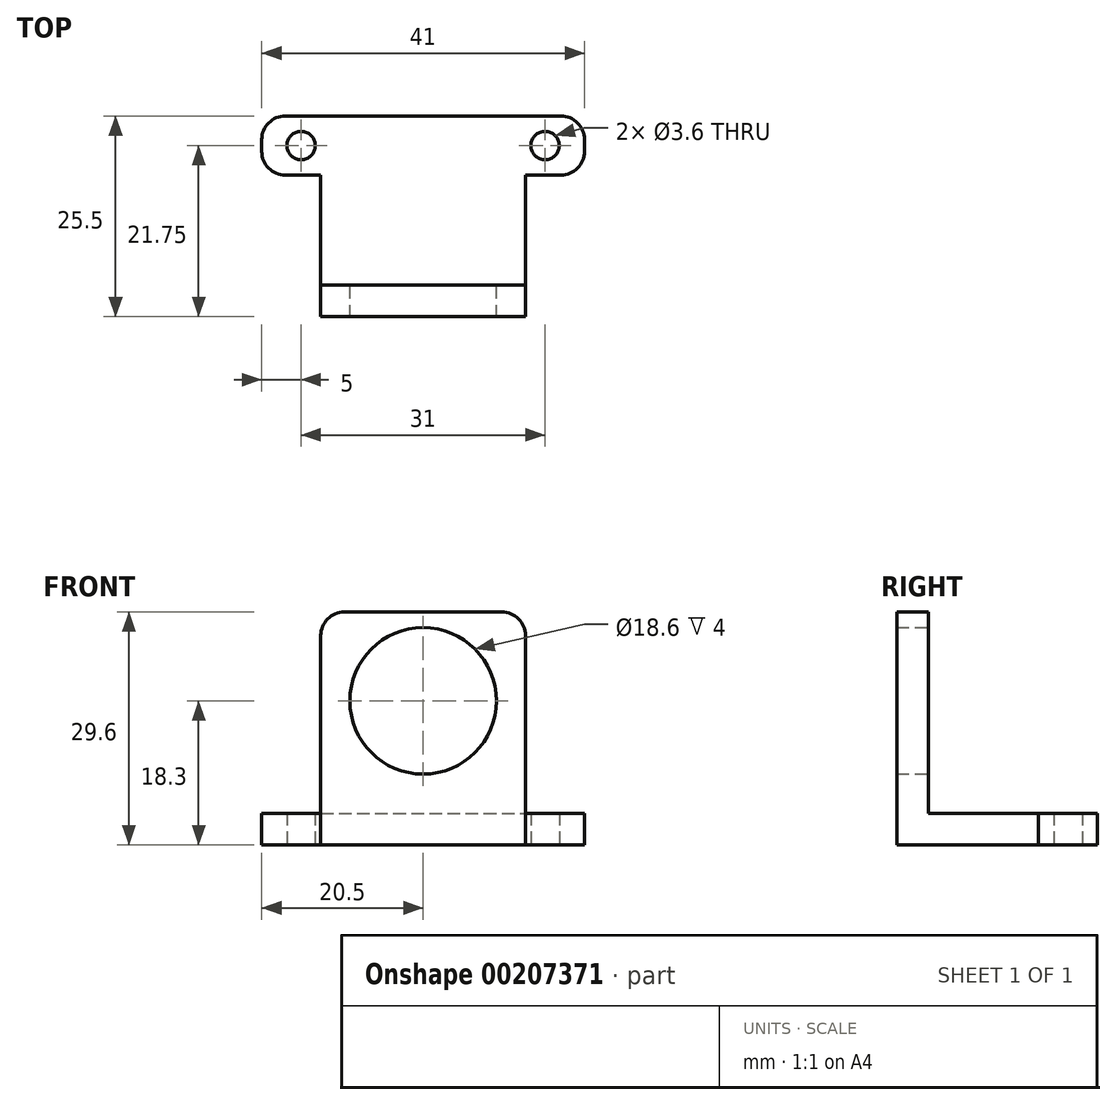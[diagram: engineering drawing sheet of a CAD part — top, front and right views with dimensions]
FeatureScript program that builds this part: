
annotation { "Feature Type Name" : "Feature", "Feature Type Description" : "" }
export const myFeature = defineFeature(function(context is Context, id is Id, definition is map)
    precondition{}
    {
        {
            var Q0;
            Q0=qCreatedBy(makeId("Top.planeOp"),FACE);
            var sketch = newSketch(context, id + "F0", { "sketchPlane" : qUnion([Q0])});
            skLineSegment(sketch, "E0.bottom", {"start": v(-41, 7.5) * mm, "end": v(0, 7.5) * mm});
            skLineSegment(sketch, "E0.top", {"start": v(-41, 0) * mm, "end": v(0, 0) * mm});
            skLineSegment(sketch, "E0.left", {"start": v(-41, 7.5) * mm, "end": v(-41, 0) * mm});
            skLineSegment(sketch, "E0.right", {"start": v(0, 7.5) * mm, "end": v(0, 0) * mm});
            skCircle(sketch, "E1", {"center": v(-36, 3.75) * mm, "radius": 1.8 * mm});
            skPoint(sketch, "E1.centerSnap0", {"position": v(-41, 3.75) * mm});
            skCircle(sketch, "E2", {"center": v(-5, 3.75) * mm, "radius": 1.8 * mm});
            skPoint(sketch, "E2.centerSnap0", {"position": v(0, 3.75) * mm});
            skLineSegment(sketch, "E3", {"start": v(-36, 3.75) * mm, "end": v(-5, 3.75) * mm, "construction": true});
            skPoint(sketch, "E4", {"position": v(-20.5, 7.5) * mm});
            skPoint(sketch, "E5", {"position": v(-20.5, 3.75) * mm});
            skLineSegment(sketch, "E6", {"start": v(-33.5, 0) * mm, "end": v(-33.5, -18) * mm});
            skLineSegment(sketch, "E7", {"start": v(-33.5, -18) * mm, "end": v(-7.5, -18) * mm});
            skLineSegment(sketch, "E8", {"start": v(-7.5, -18) * mm, "end": v(-7.5, 0) * mm});
            skPoint(sketch, "E9", {"position": v(-20.5, -18) * mm});
            skLineSegment(sketch, "E10", {"start": v(-33.5, -14) * mm, "end": v(-7.5, -14) * mm});
            skSolve(sketch);
        }
        {
            var Q0;
            Q0=makeQuery(id+"F0.imprint","IMPRINT",FACE,{"disambiguationData":[TD([[makeQuery(id+"F0.imprint","IMPRINT",EDGE,{"derivedFrom":sQuery(id+"F0.wireOp",EDGE,"E0.bottom")}),-1.0]])]});
            var Q1;
            {var subQ5=sQuery(id+"F0.wireOp",EDGE,"E10");Q1=makeQuery(id+"F0.imprint","IMPRINT",FACE,{"disambiguationData":[TD([[makeQuery(id+"F0.imprint","IMPRINT",EDGE,{"derivedFrom":subQ5}),1.0]])]});}
            extrude(context, id + "F1", {"entities" : qUnion([Q0, Q1]), "depth" : 4 * mm});
        }
        {
            var Q0;
            {var subQ0=sQuery(id+"F0.wireOp",EDGE,"E7");Q0=makeQuery(id+"F0.imprint","IMPRINT",FACE,{"disambiguationData":[TD([[makeQuery(id+"F0.imprint","IMPRINT",EDGE,{"derivedFrom":subQ0}),1.0]])]});}
            extrude(context, id + "F2", {"entities" : qUnion([Q0]), "operationType" : NewBodyOperationType.ADD, "depth" : 29.6 * mm});
        }
        {
            var Q0;
            Q0=makeQuery(id+"F2.opExtrude","SWEPT_FACE",FACE,{"disambiguationData":[OSD([sQuery(id+"F0.wireOp",EDGE,"E10")])]});
            var sketch = newSketch(context, id + "F3", { "sketchPlane" : qUnion([Q0])});
            skCircle(sketch, "E11", {"center": v(20.5, 18.3) * mm, "radius": 9.3 * mm});
            skSolve(sketch);
        }
        {
            var Q0;
            Q0=makeQuery(id+"F3.imprint","IMPRINT",FACE,{"disambiguationData":[TD([[makeQuery(id+"F3.imprint","IMPRINT",EDGE,{"derivedFrom":sQuery(id+"F3.wireOp",EDGE,"E11")}),1.0]])]});
            extrude(context, id + "F4", {"entities" : qUnion([Q0]), "operationType" : NewBodyOperationType.REMOVE, "endBound" : BoundingType.UP_TO_NEXT, "oppositeDirection" : true, "depth" : 25 * mm});
        }
        {
            var Q0;
            Q0=makeQuery(id+"F1.opExtrude","SWEPT_EDGE",EDGE,{"disambiguationData":[OSD([sQuery(id+"F0.wireOp",EDGE,"E0.top"),sQuery(id+"F0.wireOp",EDGE,"E0.right")])]});
            var Q1;
            Q1=makeQuery(id+"F1.opExtrude","SWEPT_EDGE",EDGE,{"disambiguationData":[OSD([sQuery(id+"F0.wireOp",EDGE,"E0.bottom"),sQuery(id+"F0.wireOp",EDGE,"E0.right")])]});
            var Q2;
            Q2=makeQuery(id+"F1.opExtrude","SWEPT_EDGE",EDGE,{"disambiguationData":[OSD([sQuery(id+"F0.wireOp",EDGE,"E0.top"),sQuery(id+"F0.wireOp",EDGE,"E0.left")])]});
            var Q3;
            Q3=makeQuery(id+"F1.opExtrude","SWEPT_EDGE",EDGE,{"disambiguationData":[OSD([sQuery(id+"F0.wireOp",EDGE,"E0.bottom"),sQuery(id+"F0.wireOp",EDGE,"E0.left")])]});
            var Q4;
            Q4=makeQuery(id+"F2.opExtrude","CAP_EDGE",EDGE,{"disambiguationData":[OSD([sQuery(id+"F0.wireOp",EDGE,"E6")])],"isStart":false});
            var Q5;
            Q5=makeQuery(id+"F2.opExtrude","CAP_EDGE",EDGE,{"disambiguationData":[OSD([sQuery(id+"F0.wireOp",EDGE,"E8")])],"isStart":false});
            fillet(context, id + "F5", {"entities" : qUnion([Q0, Q1, Q2, Q3, Q4, Q5]), "radius" : 3 * mm, "tangentPropagation" : true, "allowEdgeOverflow" : false});
        }
    });
